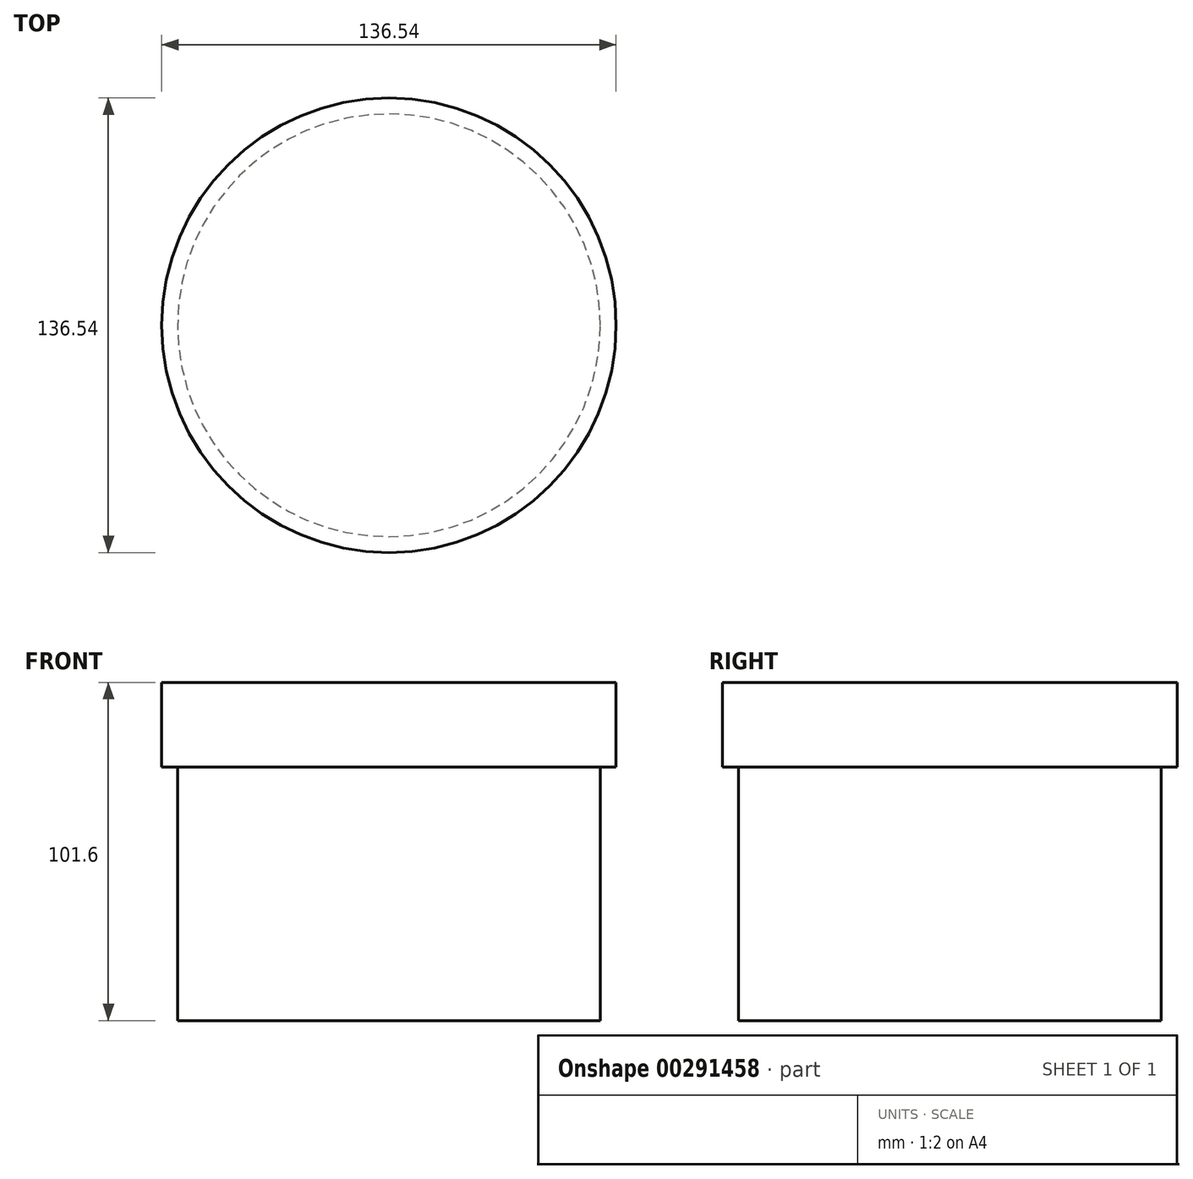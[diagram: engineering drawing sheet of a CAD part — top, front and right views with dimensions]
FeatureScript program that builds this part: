
annotation { "Feature Type Name" : "Feature", "Feature Type Description" : "" }
export const myFeature = defineFeature(function(context is Context, id is Id, definition is map)
    precondition{}
    {
        {
            var Q0;
            Q0=qCreatedBy(makeId("Front.planeOp"),FACE);
            var sketch = newSketch(context, id + "F0", { "sketchPlane" : qUnion([Q0])});
            skLineSegment(sketch, "E0", {"start": v(0, 33.9) * mm, "end": v(0, -42.3) * mm});
            skLineSegment(sketch, "E1", {"start": v(0, 33.9) * mm, "end": v(-63.5, 33.9) * mm});
            skLineSegment(sketch, "E2", {"start": v(0, 33.9) * mm, "end": v(63.5, 33.9) * mm});
            skLineSegment(sketch, "E3", {"start": v(0, -42.3) * mm, "end": v(-63.5, -42.3) * mm});
            skLineSegment(sketch, "E4", {"start": v(0, -42.3) * mm, "end": v(63.5, -42.3) * mm});
            skLineSegment(sketch, "E5", {"start": v(-63.5, 33.9) * mm, "end": v(-63.5, -42.3) * mm});
            skLineSegment(sketch, "E6", {"start": v(63.5, 33.9) * mm, "end": v(63.5, -42.3) * mm});
            skLineSegment(sketch, "E7", {"start": v(0, 33.9) * mm, "end": v(0, 59.4) * mm});
            skLineSegment(sketch, "E8", {"start": v(-63.5, 33.9) * mm, "end": v(-68.27, 33.9) * mm});
            skLineSegment(sketch, "E9.MirrorCS", {"start": v(63.5, 33.9) * mm, "end": v(68.27, 33.9) * mm});
            skLineSegment(sketch, "E10", {"start": v(-68.27, 33.9) * mm, "end": v(-68.27, 59.3) * mm});
            skLineSegment(sketch, "E11", {"start": v(-68.27, 59.3) * mm, "end": v(68.27, 59.3) * mm});
            skLineSegment(sketch, "E12", {"start": v(68.27, 59.3) * mm, "end": v(68.27, 33.9) * mm});
            skSolve(sketch);
        }
        {
            var Q0;
            Q0=makeQuery(id+"F0.imprint","IMPRINT",FACE,{"disambiguationData":[TD([[makeQuery(id+"F0.imprint","IMPRINT",EDGE,{"derivedFrom":sQuery(id+"F0.wireOp",EDGE,"E0")}),1.0]])]});
            var Q1;
            Q1=sQuery(id+"F0.wireOp",EDGE,"E0");
            revolve(context, id + "F1", {"entities" : qUnion([Q0]), "axis" : qUnion([Q1]), "revolveType" : RevolveType.FULL});
        }
        {
            var Q0;
            {var subQ4=sQuery(id+"F0.wireOp",EDGE,"E2");Q0=makeQuery(id+"F0.imprint","IMPRINT",FACE,{"disambiguationData":[TD([[makeQuery(id+"F0.imprint","IMPRINT",EDGE,{"derivedFrom":subQ4}),1.0]])]});}
            var Q1;
            Q1=sQuery(id+"F0.wireOp",EDGE,"E7");
            revolve(context, id + "F2", {"operationType" : NewBodyOperationType.ADD, "entities" : qUnion([Q0]), "axis" : qUnion([Q1]), "revolveType" : RevolveType.FULL});
        }
    });
